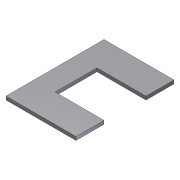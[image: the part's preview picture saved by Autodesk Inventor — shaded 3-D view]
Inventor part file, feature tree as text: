
AUTODESK INVENTOR PART (.ipt)
format: ipt  version: 2012 (Build 160160000, 160)  size: 84,480 bytes
history: native  units: in
note: dims shown in document units (in); Inventor stores cm internally (conversion verified against a paired STEP export)
features: extrude x2, sketch x2
ambient origin geometry x8: Origin, YZ Plane, XZ Plane, XY Plane, X Axis, Y Axis, Z Axis, Center Point
bodies: Solid1 (feature_tree)
feature tree (4):
  extrude  "Extrusion1"  Depth=0.25in
  extrude  "Extrusion2"  Depth=3.0in
  sketch  "Sketch1"  dims[d0=0.95in d1=0.25in]
  sketch  "Sketch2"  dims[d2=7.0in d3=0.0in d4=3.0in d6=7.0in d7=0.0in d8=1.5in d9=5.0in]
